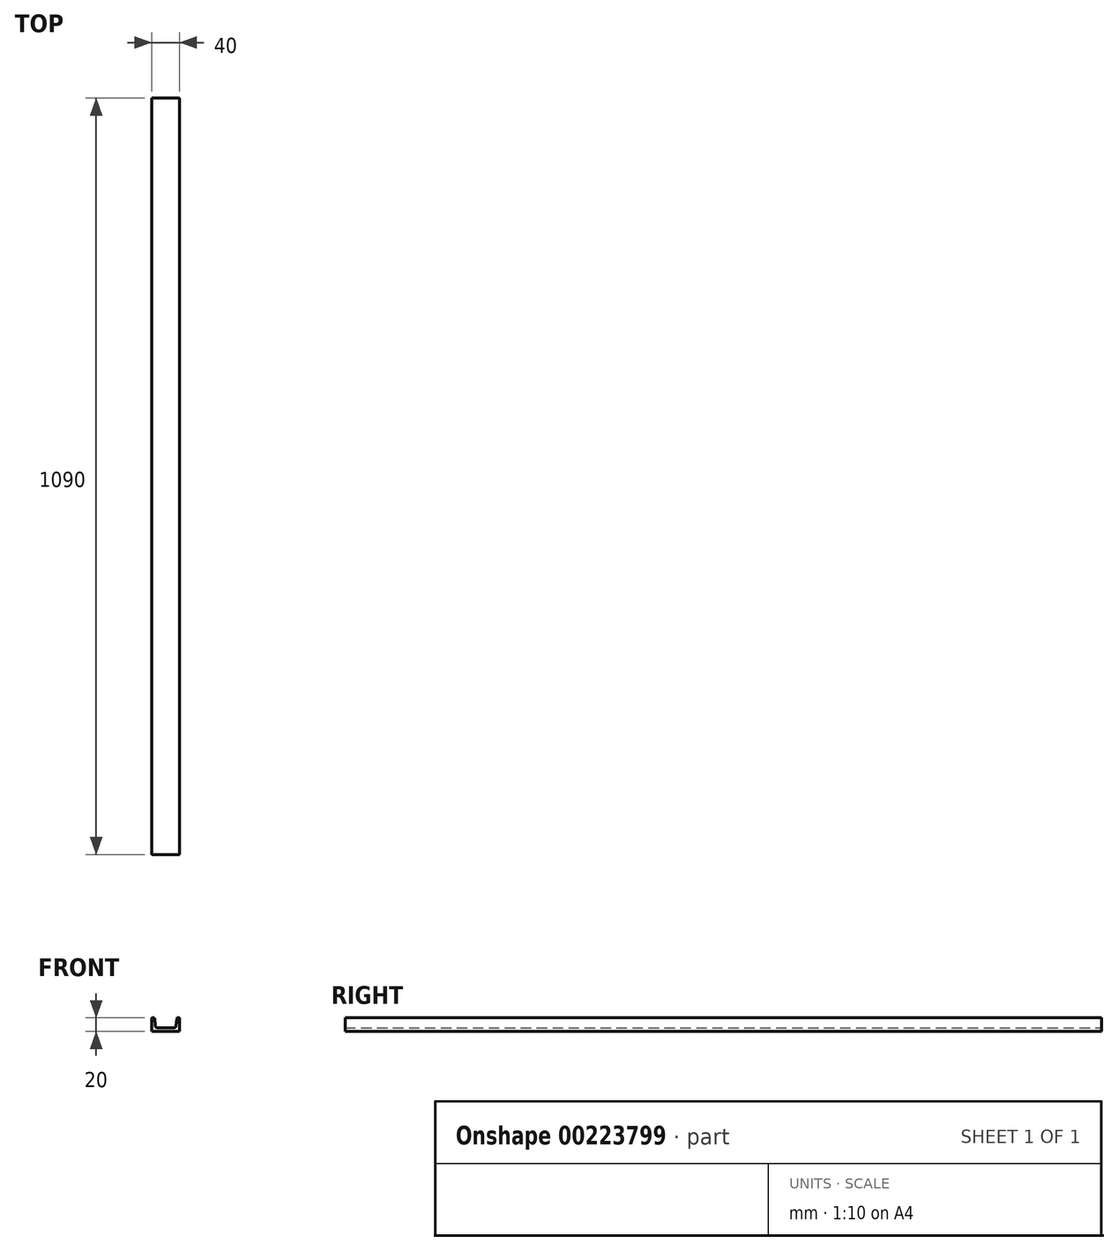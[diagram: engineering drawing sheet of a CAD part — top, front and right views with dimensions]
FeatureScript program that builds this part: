
annotation { "Feature Type Name" : "Feature", "Feature Type Description" : "" }
export const myFeature = defineFeature(function(context is Context, id is Id, definition is map)
    precondition{}
    {
        {
            var Q0;
            Q0=qCreatedBy(makeId("Front.planeOp"),FACE);
            var sketch = newSketch(context, id + "F0", { "sketchPlane" : qUnion([Q0])});
            skLineSegment(sketch, "E0", {"start": v(-29.96, 0) * mm, "end": v(10.04, 0) * mm});
            skLineSegment(sketch, "E1", {"start": v(10.04, 0) * mm, "end": v(10.04, 19) * mm});
            skLineSegment(sketch, "E2", {"start": v(9.04, 20) * mm, "end": v(7.92, 20) * mm});
            skLineSegment(sketch, "E3", {"start": v(5.92, 18.13) * mm, "end": v(5.32, 8.74) * mm});
            skLineSegment(sketch, "E4", {"start": v(1.32, 5) * mm, "end": v(-21.16, 5) * mm});
            skLineSegment(sketch, "E5", {"start": v(-25.15, 8.76) * mm, "end": v(-25.72, 18.12) * mm});
            skLineSegment(sketch, "E6", {"start": v(-27.72, 20) * mm, "end": v(-28.84, 20) * mm});
            skLineSegment(sketch, "E7", {"start": v(-29.84, 19) * mm, "end": v(-29.96, 0) * mm});
            skPoint(sketch, "E8.visualSharp", {"position": v(-29.84, 20) * mm});
            skArc(sketch, "E8.filletArc", {"start": v(-28.84, 20) * mm, "mid": v(-29.55, 19.7) * mm, "end": v(-29.84, 19) * mm});
            skPoint(sketch, "E9.visualSharp", {"position": v(-25.84, 20) * mm});
            skArc(sketch, "E9.filletArc", {"start": v(-25.72, 18.12) * mm, "mid": v(-26.35, 19.46) * mm, "end": v(-27.72, 20) * mm});
            skPoint(sketch, "E10.visualSharp", {"position": v(6.04, 20) * mm});
            skArc(sketch, "E10.filletArc", {"start": v(7.92, 20) * mm, "mid": v(6.55, 19.46) * mm, "end": v(5.92, 18.13) * mm});
            skPoint(sketch, "E11.visualSharp", {"position": v(10.04, 20) * mm});
            skArc(sketch, "E11.filletArc", {"start": v(10.04, 19) * mm, "mid": v(9.75, 19.7) * mm, "end": v(9.04, 20) * mm});
            skPoint(sketch, "E12.visualSharp", {"position": v(-24.93, 5) * mm});
            skArc(sketch, "E12.filletArc", {"start": v(-25.15, 8.76) * mm, "mid": v(-23.9, 6.09) * mm, "end": v(-21.16, 5) * mm});
            skPoint(sketch, "E13.visualSharp", {"position": v(5.07, 5) * mm});
            skArc(sketch, "E13.filletArc", {"start": v(1.32, 5) * mm, "mid": v(4.06, 6.08) * mm, "end": v(5.32, 8.74) * mm});
            skSolve(sketch);
        }
        {
            var Q0;
            Q0=makeQuery(id+"F0.imprint","IMPRINT",FACE,{"disambiguationData":[TD([[makeQuery(id+"F0.imprint","IMPRINT",EDGE,{"derivedFrom":sQuery(id+"F0.wireOp",EDGE,"E0")}),1.0]])]});
            extrude(context, id + "F1", {"entities" : qUnion([Q0]), "depth" : 1090 * mm});
        }
    });
